# Revit family: Class-II-Fan_VBBB-CCW-UBD_Carnes
name_source: partatom
category: Mechanical Equipment
revit_build: Autodesk Revit Architecture 2012 (Build: 20110309_2315(x64)
units: mm (PartAtom-declared; Revit-internal decimal feet)

## types (1)
- See Type Catalog
    001 = 21.6 "
    04 CSI = 23 34 23
    95 CSI = 15830
    A = 13 "
    Angle = 360.00°
    Assembly Code = D3040200
    B = 9.8 "
    C = 13.3 "
    Catalog URL = http://www.carnes.com
    D = 17.6 "
    DX = 1 "
    Default Elevation = 0 "
    Description = Cetrifugal Blowers
    Drip = 4.9 "
    Drip1 = 4.9 "
    G = 16 "
    H = 32 "
    HA = 9.8 "
    HC = 13.9 "
    HE = 10.6 "
    HG = 9.3 "
    HJ = 9.3 "
    HN = 12.9 "
    Housing = Aluminum-Carnes-Spun-Brushed
    IOM Instructions URL = http://www.carnes.com
    J = 7.4 "
    KL = 2 "
    Manufacturer = Carnes Company
    Manufacturer Fax = 608-845-6470
    Model = VBBB 12
    Motor Cover = No
    Motor Pedastal Stand = 18.6 "
    P = 26.5 "
    Product Page URL = http://www.carnes.com
    Radius = 6.6 "
    SD = 1.2 "
    SD Radius = 0.6 "
    SE = 2.8 "
    Support Plate Drip = 17.6 "
    URL = http://www.carnes.com
    Warranty URL = http://www.carnes.com
    Weather Cover = Yes
    Weather Cover Height = 22.4 "
    Weather Cover Length = 23.4 "
    Weather Cover Width = 13 "
    ecoScorecard Product Page = http://ecoscorecard.com

## geometry (parser evidence)
native form markers: Blend x2, Sweep x35
no freeform markers — native parametric forms only
